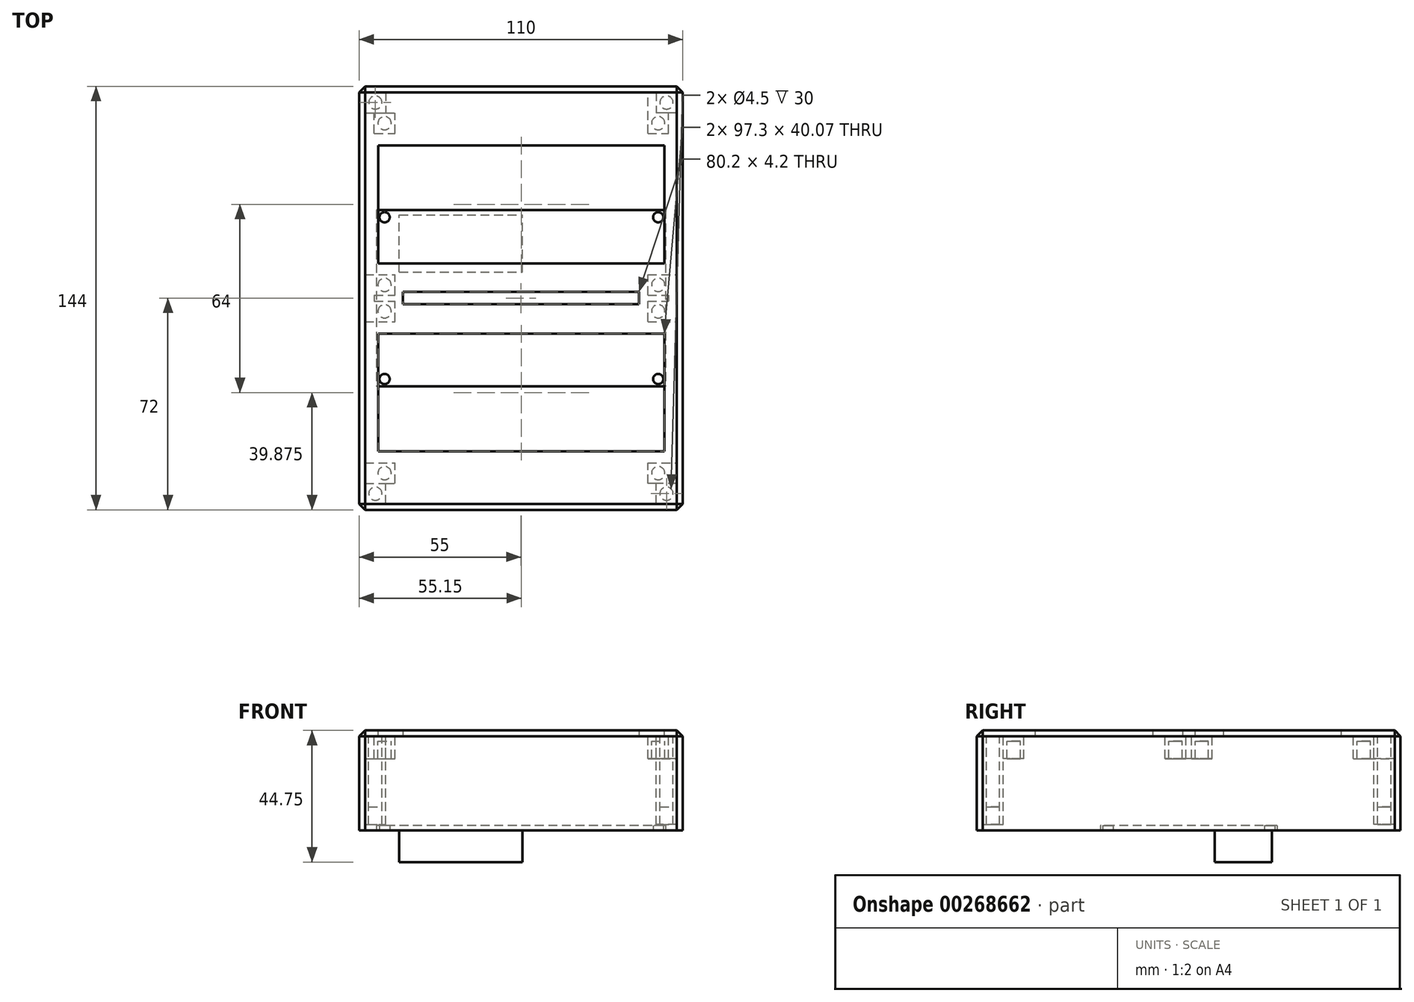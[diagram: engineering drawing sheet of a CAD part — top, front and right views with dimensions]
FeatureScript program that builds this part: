
annotation { "Feature Type Name" : "Feature", "Feature Type Description" : "" }
export const myFeature = defineFeature(function(context is Context, id is Id, definition is map)
    precondition{}
    {
        {
            var Q0;
            Q0=qCreatedBy(makeId("Top.planeOp"),FACE);
            var sketch = newSketch(context, id + "F0", { "sketchPlane" : qUnion([Q0])});
            skLineSegment(sketch, "E0.bottom", {"start": v(49.15, 30) * mm, "end": v(-49.15, 30) * mm});
            skLineSegment(sketch, "E0.top", {"start": v(49.15, -30) * mm, "end": v(-49.15, -30) * mm});
            skLineSegment(sketch, "E0.left", {"start": v(49.15, 30) * mm, "end": v(49.15, -30) * mm});
            skLineSegment(sketch, "E0.right", {"start": v(-49.15, 30) * mm, "end": v(-49.15, -30) * mm});
            skPoint(sketch, "E0.middle", {"position": v(0, 0) * mm});
            skCircle(sketch, "E1", {"center": v(46.65, 27.5) * mm, "radius": 1.75 * mm});
            skCircle(sketch, "E2.MirrorC", {"center": v(46.65, -27.5) * mm, "radius": 1.75 * mm});
            skCircle(sketch, "E3", {"center": v(-46.35, 27.5) * mm, "radius": 1.75 * mm});
            skCircle(sketch, "E4.MirrorC", {"center": v(-46.35, -27.5) * mm, "radius": 1.75 * mm});
            skSolve(sketch);
        }
        {
            var Q0;
            Q0=makeQuery(id+"F0.imprint","IMPRINT",FACE,{"disambiguationData":[TD([[makeQuery(id+"F0.imprint","IMPRINT",EDGE,{"derivedFrom":sQuery(id+"F0.wireOp",EDGE,"E0.bottom")}),1.0]])]});
            var Q1;
            Q1=makeQuery(id+"F0.imprint","IMPRINT",FACE,{"disambiguationData":[TD([[makeQuery(id+"F0.imprint","IMPRINT",EDGE,{"derivedFrom":sQuery(id+"F0.wireOp",EDGE,"rkxBa0un-ti2P-H2wi-MoX2-qtd8EblVNG1E.bottom")}),-1.0]])]});
            extrude(context, id + "F1", {"entities" : qUnion([Q0, Q1]), "depth" : 1.6 * mm});
        }
        {
            var Q0;
            Q0=makeQuery(id+"F1.opExtrude","CAP_FACE",FACE,{"disambiguationData":[OSD([sQuery(id+"F0.wireOp",EDGE,"E0.bottom"),sQuery(id+"F0.wireOp",EDGE,"E0.top"),sQuery(id+"F0.wireOp",EDGE,"E0.left"),sQuery(id+"F0.wireOp",EDGE,"E0.right"),sQuery(id+"F0.wireOp",EDGE,"E1"),sQuery(id+"F0.wireOp",EDGE,"E2.MirrorC"),sQuery(id+"F0.wireOp",EDGE,"E3"),sQuery(id+"F0.wireOp",EDGE,"E4.MirrorC")])],"isStart":false});
            var sketch = newSketch(context, id + "F2", { "sketchPlane" : qUnion([Q0])});
            skLineSegment(sketch, "E5.bottom", {"start": v(-48.4, 19.81) * mm, "end": v(48.7, 19.81) * mm});
            skLineSegment(sketch, "E5.top", {"start": v(-48.4, -20.06) * mm, "end": v(48.7, -20.06) * mm});
            skLineSegment(sketch, "E5.left", {"start": v(-48.4, 19.81) * mm, "end": v(-48.4, -20.06) * mm});
            skLineSegment(sketch, "E5.right", {"start": v(48.7, 19.81) * mm, "end": v(48.7, -20.06) * mm});
            skSolve(sketch);
        }
        {
            var Q0;
            Q0=makeQuery(id+"F2.imprint","IMPRINT",FACE,{"disambiguationData":[TD([[makeQuery(id+"F2.imprint","IMPRINT",EDGE,{"derivedFrom":sQuery(id+"F2.wireOp",EDGE,"E5.bottom")}),-1.0]])]});
            extrude(context, id + "F3", {"entities" : qUnion([Q0]), "depth" : 9.9 * mm});
        }
        {
            var Q0;
            Q0=makeQuery(id+"F0.imprint","IMPRINT",FACE,{"disambiguationData":[TD([[makeQuery(id+"F0.imprint","IMPRINT",EDGE,{"derivedFrom":sQuery(id+"F0.wireOp",EDGE,"E0.bottom")}),1.0]])]});
            var sketch = newSketch(context, id + "F4", { "sketchPlane" : qUnion([Q0])});
            skLineSegment(sketch, "E6.bottom", {"start": v(-41.35, 8.84) * mm, "end": v(0.58, 8.84) * mm});
            skLineSegment(sketch, "E6.top", {"start": v(-41.35, 28.34) * mm, "end": v(0.58, 28.34) * mm});
            skLineSegment(sketch, "E6.left", {"start": v(-41.35, 8.84) * mm, "end": v(-41.35, 28.34) * mm});
            skLineSegment(sketch, "E6.right", {"start": v(0.58, 8.84) * mm, "end": v(0.58, 28.34) * mm});
            skSolve(sketch);
        }
        {
            var Q0;
            Q0=makeQuery(id+"F4.imprint","IMPRINT",FACE,{"disambiguationData":[TD([[makeQuery(id+"F4.imprint","IMPRINT",EDGE,{"derivedFrom":sQuery(id+"F4.wireOp",EDGE,"E6.bottom")}),1.0]])]});
            extrude(context, id + "F5", {"entities" : qUnion([Q0]), "oppositeDirection" : true, "depth" : 10.75 * mm});
        }
        {
            var Q0;
            Q0=makeQuery(id+"F3.opExtrude","SWEPT_BODY",BODY,{"disambiguationData":[OSD([sQuery(id+"F2.wireOp",EDGE,"E5.bottom"),sQuery(id+"F2.wireOp",EDGE,"E5.top"),sQuery(id+"F2.wireOp",EDGE,"E5.left"),sQuery(id+"F2.wireOp",EDGE,"E5.right")])]});
            transform(context, id + "F6", {"entities" : qUnion([Q0]), "transformType" : TransformType.TRANSLATION_3D, "dx" : 0 * mm, "dy" : 0 * mm, "dz" : 0 * mm, "makeCopy" : true});
        }
        {
            var Q0;
            Q0=qCreatedBy(makeId("Top.planeOp"),FACE);
            var sketch = newSketch(context, id + "F7", { "sketchPlane" : qUnion([Q0])});
            skLineSegment(sketch, "E7.bottom", {"start": v(55, -72) * mm, "end": v(-55, -72) * mm});
            skLineSegment(sketch, "E7.top", {"start": v(55, 72) * mm, "end": v(-55, 72) * mm});
            skLineSegment(sketch, "E7.left", {"start": v(55, -72) * mm, "end": v(55, 72) * mm});
            skLineSegment(sketch, "E7.right", {"start": v(-55, -72) * mm, "end": v(-55, 72) * mm});
            skPoint(sketch, "E7.middle", {"position": v(0, 0) * mm});
            skSolve(sketch);
        }
        {
            var Q0;
            Q0 = qSketchRegion(id + "F7", true);
            extrude(context, id + "F8", {"entities" : qUnion([Q0]), "depth" : 34 * mm});
        }
        {
            var Q0;
            Q0=makeQuery(id+"F8.opExtrude","CAP_FACE",FACE,{"disambiguationData":[OSD([sQuery(id+"F7.wireOp",EDGE,"E7.bottom"),sQuery(id+"F7.wireOp",EDGE,"E7.top"),sQuery(id+"F7.wireOp",EDGE,"E7.left"),sQuery(id+"F7.wireOp",EDGE,"E7.right")])],"isStart":true});
            shell(context, id + "F9", {"entities" : qUnion([Q0]), "thickness" : 2 * mm});
        }
        {
            var Q0;
            Q0=makeQuery(id+"F8.opExtrude","CAP_FACE",FACE,{"disambiguationData":[OSD([sQuery(id+"F7.wireOp",EDGE,"E7.bottom"),sQuery(id+"F7.wireOp",EDGE,"E7.top"),sQuery(id+"F7.wireOp",EDGE,"E7.left"),sQuery(id+"F7.wireOp",EDGE,"E7.right")])],"isStart":false});
            var Q1;
            Q1=makeQuery(id+"F8.opExtrude","SWEPT_EDGE",EDGE,{"disambiguationData":[OSD([sQuery(id+"F7.wireOp",EDGE,"E7.bottom"),sQuery(id+"F7.wireOp",EDGE,"E7.left")])]});
            var Q2;
            Q2=makeQuery(id+"F8.opExtrude","SWEPT_EDGE",EDGE,{"disambiguationData":[OSD([sQuery(id+"F7.wireOp",EDGE,"E7.top"),sQuery(id+"F7.wireOp",EDGE,"E7.left")])]});
            var Q3;
            Q3=makeQuery(id+"F8.opExtrude","SWEPT_EDGE",EDGE,{"disambiguationData":[OSD([sQuery(id+"F7.wireOp",EDGE,"E7.top"),sQuery(id+"F7.wireOp",EDGE,"E7.right")])]});
            var Q4;
            Q4=makeQuery(id+"F8.opExtrude","SWEPT_EDGE",EDGE,{"disambiguationData":[OSD([sQuery(id+"F7.wireOp",EDGE,"E7.bottom"),sQuery(id+"F7.wireOp",EDGE,"E7.right")])]});
            chamfer(context, id + "F10", {"entities" : qUnion([Q0, Q1, Q2, Q3, Q4]), "width" : 2 * mm, "tangentPropagation" : true});
        }
        {
            var Q0;
            Q0=makeQuery(id+"F3.opExtrude","SWEPT_BODY",BODY,{"disambiguationData":[OSD([sQuery(id+"F2.wireOp",EDGE,"E5.bottom"),sQuery(id+"F2.wireOp",EDGE,"E5.top"),sQuery(id+"F2.wireOp",EDGE,"E5.left"),sQuery(id+"F2.wireOp",EDGE,"E5.right")])]});
            transform(context, id + "F11", {"entities" : qUnion([Q0]), "transformType" : TransformType.TRANSLATION_3D, "dx" : 0 * mm, "dy" : 32 * mm, "dz" : 22.4 * mm, "makeCopy" : false});
        }
        {
            var Q0;
            Q0=makeQuery(id+"F6.opPattern","COPY",BODY,{"derivedFrom":makeQuery(id+"F3.opExtrude","SWEPT_BODY",BODY,{"disambiguationData":[OSD([sQuery(id+"F2.wireOp",EDGE,"E5.bottom"),sQuery(id+"F2.wireOp",EDGE,"E5.top"),sQuery(id+"F2.wireOp",EDGE,"E5.left"),sQuery(id+"F2.wireOp",EDGE,"E5.right")])]}),"instanceName":"1"});
            transform(context, id + "F12", {"entities" : qUnion([Q0]), "transformType" : TransformType.TRANSLATION_3D, "dx" : 0 * mm, "dy" : -32 * mm, "dz" : 22.4 * mm, "makeCopy" : false});
        }
        {
            var Q0;
            Q0=makeQuery(id+"F8.opExtrude","CAP_FACE",FACE,{"disambiguationData":[OSD([sQuery(id+"F7.wireOp",EDGE,"E7.bottom"),sQuery(id+"F7.wireOp",EDGE,"E7.top"),sQuery(id+"F7.wireOp",EDGE,"E7.left"),sQuery(id+"F7.wireOp",EDGE,"E7.right")])],"isStart":false});
            cPlane(context, id + "F13", {"entities" : qUnion([Q0]), "cplaneType" : CPlaneType.OFFSET, "offset" : 0 * mm, "width" : 150 * mm, "height" : 150 * mm});
        }
        {
            var Q0;
            Q0=qCreatedBy(id+"F13.planeOp",FACE);
            var sketch = newSketch(context, id + "F14", { "sketchPlane" : qUnion([Q0])});
            skLineSegment(sketch, "E8.0.0", {"start": v(-48.4, 51.81) * mm, "end": v(-48.4, 11.94) * mm});
            skLineSegment(sketch, "E8.0.1", {"start": v(-48.4, 11.94) * mm, "end": v(48.7, 11.94) * mm});
            skLineSegment(sketch, "E8.0.2", {"start": v(48.7, 11.94) * mm, "end": v(48.7, 51.81) * mm});
            skLineSegment(sketch, "E8.0.3", {"start": v(48.7, 51.81) * mm, "end": v(-48.4, 51.81) * mm});
            skLineSegment(sketch, "E9.0.0", {"start": v(-48.4, -12.19) * mm, "end": v(-48.4, -52.06) * mm});
            skLineSegment(sketch, "E9.0.1", {"start": v(-48.4, -52.06) * mm, "end": v(48.7, -52.06) * mm});
            skLineSegment(sketch, "E9.0.2", {"start": v(48.7, -52.06) * mm, "end": v(48.7, -12.19) * mm});
            skLineSegment(sketch, "E9.0.3", {"start": v(48.7, -12.19) * mm, "end": v(-48.4, -12.19) * mm});
            skCircle(sketch, "E10.0", {"center": v(-46.35, -4.5) * mm, "radius": 1.75 * mm});
            skCircle(sketch, "E11.0", {"center": v(-46.35, 4.5) * mm, "radius": 1.75 * mm});
            skCircle(sketch, "E12.0", {"center": v(46.65, 4.5) * mm, "radius": 1.75 * mm});
            skCircle(sketch, "E13.0", {"center": v(46.65, -4.5) * mm, "radius": 1.75 * mm});
            skCircle(sketch, "E14.0", {"center": v(46.65, -59.5) * mm, "radius": 1.75 * mm});
            skCircle(sketch, "E15.0", {"center": v(-46.35, -59.5) * mm, "radius": 1.75 * mm});
            skCircle(sketch, "E16.0", {"center": v(-46.35, 59.5) * mm, "radius": 1.75 * mm});
            skCircle(sketch, "E17.0", {"center": v(46.65, 59.5) * mm, "radius": 1.75 * mm});
            skLineSegment(sketch, "E18.MirrorCS", {"start": v(48.7, 91.68) * mm, "end": v(48.7, 51.81) * mm});
            skLineSegment(sketch, "E19.0", {"start": v(48.8, 51.91) * mm, "end": v(-48.5, 51.91) * mm});
            skLineSegment(sketch, "E19.1", {"start": v(48.8, 11.84) * mm, "end": v(48.8, 51.91) * mm});
            skLineSegment(sketch, "E19.2", {"start": v(-48.5, 11.84) * mm, "end": v(48.8, 11.84) * mm});
            skLineSegment(sketch, "E19.3", {"start": v(-48.5, 51.91) * mm, "end": v(-48.5, 11.84) * mm});
            skLineSegment(sketch, "E20.0", {"start": v(48.8, -12.09) * mm, "end": v(-48.5, -12.09) * mm});
            skLineSegment(sketch, "E20.1", {"start": v(48.8, -52.16) * mm, "end": v(48.8, -12.09) * mm});
            skLineSegment(sketch, "E20.2", {"start": v(-48.5, -52.16) * mm, "end": v(48.8, -52.16) * mm});
            skLineSegment(sketch, "E20.3", {"start": v(-48.5, -12.09) * mm, "end": v(-48.5, -52.16) * mm});
            skSolve(sketch);
        }
        {
            var Q0;
            Q0=makeQuery(id+"F14.imprint","IMPRINT",FACE,{"disambiguationData":[TD([[makeQuery(id+"F14.imprint","IMPRINT",EDGE,{"derivedFrom":sQuery(id+"F14.wireOp",EDGE,"E8.0.0")}),-1.0]])]});
            var Q1;
            Q1=makeQuery(id+"F14.imprint","IMPRINT",FACE,{"disambiguationData":[TD([[makeQuery(id+"F14.imprint","IMPRINT",EDGE,{"derivedFrom":sQuery(id+"F14.wireOp",EDGE,"E8.0.0")}),1.0]])]});
            var Q2;
            Q2=makeQuery(id+"F14.imprint","IMPRINT",FACE,{"disambiguationData":[TD([[makeQuery(id+"F14.imprint","IMPRINT",EDGE,{"derivedFrom":sQuery(id+"F14.wireOp",EDGE,"E9.0.0")}),-1.0]])]});
            var Q3;
            Q3=makeQuery(id+"F14.imprint","IMPRINT",FACE,{"disambiguationData":[TD([[makeQuery(id+"F14.imprint","IMPRINT",EDGE,{"derivedFrom":sQuery(id+"F14.wireOp",EDGE,"E9.0.0")}),1.0]])]});
            var Q4;
            Q4=sQuery(id+"F14.wireOp",EDGE,"E19.3");
            var Q5;
            Q5=sQuery(id+"F14.wireOp",EDGE,"E19.2");
            var Q6;
            Q6=sQuery(id+"F14.wireOp",EDGE,"E19.1");
            var Q7;
            Q7=sQuery(id+"F14.wireOp",EDGE,"E19.0");
            extrude(context, id + "F15", {"entities" : qUnion([Q0, Q1, Q2, Q3]), "operationType" : NewBodyOperationType.REMOVE, "surfaceEntities" : qUnion([Q4, Q5, Q6, Q7]), "oppositeDirection" : true, "depth" : 25 * mm});
        }
        {
            var Q0;
            Q0=makeQuery(id+"F9.opShell","OFFSET_FACE",FACE,{"disambiguationData":[OSD([sQuery(id+"F7.wireOp",EDGE,"E7.bottom"),sQuery(id+"F7.wireOp",EDGE,"E7.top"),sQuery(id+"F7.wireOp",EDGE,"E7.left"),sQuery(id+"F7.wireOp",EDGE,"E7.right")])]});
            cPlane(context, id + "F16", {"entities" : qUnion([Q0]), "cplaneType" : CPlaneType.OFFSET, "offset" : 0 * mm, "width" : 150 * mm, "height" : 150 * mm});
        }
        {
            var Q0;
            Q0=qCreatedBy(id+"F16.planeOp",FACE);
            var sketch = newSketch(context, id + "F17", { "sketchPlane" : qUnion([Q0])});
            skLineSegment(sketch, "E21.bottom", {"start": v(-53, 70) * mm, "end": v(-46, 70) * mm});
            skLineSegment(sketch, "E21.top", {"start": v(-53, 63) * mm, "end": v(-46, 63) * mm});
            skLineSegment(sketch, "E21.left", {"start": v(-53, 70) * mm, "end": v(-53, 63) * mm});
            skLineSegment(sketch, "E21.right", {"start": v(-46, 70) * mm, "end": v(-46, 63) * mm});
            skLineSegment(sketch, "E22.MirrorCS", {"start": v(46, 70) * mm, "end": v(46, 63) * mm});
            skLineSegment(sketch, "E23.MirrorCS", {"start": v(53, 70) * mm, "end": v(46, 70) * mm});
            skLineSegment(sketch, "E24.MirrorCS", {"start": v(53, 70) * mm, "end": v(53, 63) * mm});
            skLineSegment(sketch, "E25.MirrorCS", {"start": v(53, 63) * mm, "end": v(46, 63) * mm});
            skLineSegment(sketch, "E26.MirrorCS", {"start": v(-53, -63) * mm, "end": v(-46, -63) * mm});
            skLineSegment(sketch, "E27.MirrorCS", {"start": v(-53, -70) * mm, "end": v(-53, -63) * mm});
            skLineSegment(sketch, "E28.MirrorCS", {"start": v(-53, -70) * mm, "end": v(-46, -70) * mm});
            skLineSegment(sketch, "E29.MirrorCS", {"start": v(-46, -70) * mm, "end": v(-46, -63) * mm});
            skLineSegment(sketch, "E30.MirrorCS", {"start": v(46, -70) * mm, "end": v(46, -63) * mm});
            skLineSegment(sketch, "E31.MirrorCS", {"start": v(53, -70) * mm, "end": v(46, -70) * mm});
            skLineSegment(sketch, "E32.MirrorCS", {"start": v(53, -70) * mm, "end": v(53, -63) * mm});
            skLineSegment(sketch, "E33.MirrorCS", {"start": v(53, -63) * mm, "end": v(46, -63) * mm});
            skCircle(sketch, "E34", {"center": v(49.5, -66.5) * mm, "radius": 2.25 * mm});
            skCircle(sketch, "E35.MirrorC", {"center": v(-49.5, -66.5) * mm, "radius": 2.25 * mm});
            skCircle(sketch, "E36.MirrorC", {"center": v(49.5, 66.5) * mm, "radius": 2.25 * mm});
            skCircle(sketch, "E37.MirrorC", {"center": v(-49.5, 66.5) * mm, "radius": 2.25 * mm});
            skLineSegment(sketch, "E38.bottom", {"start": v(43.15, -56) * mm, "end": v(50.15, -56) * mm});
            skLineSegment(sketch, "E38.top", {"start": v(43.15, -63) * mm, "end": v(50.15, -63) * mm});
            skLineSegment(sketch, "E38.left", {"start": v(43.15, -56) * mm, "end": v(43.15, -63) * mm});
            skLineSegment(sketch, "E38.right", {"start": v(50.15, -56) * mm, "end": v(50.15, -63) * mm});
            skPoint(sketch, "E38.middle", {"position": v(46.65, -59.5) * mm});
            skLineSegment(sketch, "E39.bottom", {"start": v(-49.85, -56) * mm, "end": v(-42.85, -56) * mm});
            skLineSegment(sketch, "E39.top", {"start": v(-49.85, -63) * mm, "end": v(-42.85, -63) * mm});
            skLineSegment(sketch, "E39.left", {"start": v(-49.85, -56) * mm, "end": v(-49.85, -63) * mm});
            skLineSegment(sketch, "E39.right", {"start": v(-42.85, -56) * mm, "end": v(-42.85, -63) * mm});
            skPoint(sketch, "E39.middle", {"position": v(-46.35, -59.5) * mm});
            skLineSegment(sketch, "E40.bottom", {"start": v(-49.85, -1) * mm, "end": v(-42.85, -1) * mm});
            skLineSegment(sketch, "E40.top", {"start": v(-49.85, -8) * mm, "end": v(-42.85, -8) * mm});
            skLineSegment(sketch, "E40.left", {"start": v(-49.85, -1) * mm, "end": v(-49.85, -8) * mm});
            skLineSegment(sketch, "E40.right", {"start": v(-42.85, -1) * mm, "end": v(-42.85, -8) * mm});
            skPoint(sketch, "E40.middle", {"position": v(-46.35, -4.5) * mm});
            skLineSegment(sketch, "E41.bottom", {"start": v(-49.85, 8) * mm, "end": v(-42.85, 8) * mm});
            skLineSegment(sketch, "E41.top", {"start": v(-49.85, 1) * mm, "end": v(-42.85, 1) * mm});
            skLineSegment(sketch, "E41.left", {"start": v(-49.85, 8) * mm, "end": v(-49.85, 1) * mm});
            skLineSegment(sketch, "E41.right", {"start": v(-42.85, 8) * mm, "end": v(-42.85, 1) * mm});
            skPoint(sketch, "E41.middle", {"position": v(-46.35, 4.5) * mm});
            skLineSegment(sketch, "E42.bottom", {"start": v(43.15, -1) * mm, "end": v(50.15, -1) * mm});
            skLineSegment(sketch, "E42.top", {"start": v(43.15, -8) * mm, "end": v(50.15, -8) * mm});
            skLineSegment(sketch, "E42.left", {"start": v(43.15, -1) * mm, "end": v(43.15, -8) * mm});
            skLineSegment(sketch, "E42.right", {"start": v(50.15, -1) * mm, "end": v(50.15, -8) * mm});
            skPoint(sketch, "E42.middle", {"position": v(46.65, -4.5) * mm});
            skLineSegment(sketch, "E43.bottom", {"start": v(43.15, 8) * mm, "end": v(50.15, 8) * mm});
            skLineSegment(sketch, "E43.top", {"start": v(43.15, 1) * mm, "end": v(50.15, 1) * mm});
            skLineSegment(sketch, "E43.left", {"start": v(43.15, 8) * mm, "end": v(43.15, 1) * mm});
            skLineSegment(sketch, "E43.right", {"start": v(50.15, 8) * mm, "end": v(50.15, 1) * mm});
            skPoint(sketch, "E43.middle", {"position": v(46.65, 4.5) * mm});
            skLineSegment(sketch, "E44.bottom", {"start": v(-49.85, 63) * mm, "end": v(-42.85, 63) * mm});
            skLineSegment(sketch, "E44.top", {"start": v(-49.85, 56) * mm, "end": v(-42.85, 56) * mm});
            skLineSegment(sketch, "E44.left", {"start": v(-49.85, 63) * mm, "end": v(-49.85, 56) * mm});
            skLineSegment(sketch, "E44.right", {"start": v(-42.85, 63) * mm, "end": v(-42.85, 56) * mm});
            skPoint(sketch, "E44.middle", {"position": v(-46.35, 59.5) * mm});
            skLineSegment(sketch, "E45.bottom", {"start": v(43.15, 63) * mm, "end": v(50.15, 63) * mm});
            skLineSegment(sketch, "E45.top", {"start": v(43.15, 56) * mm, "end": v(50.15, 56) * mm});
            skLineSegment(sketch, "E45.left", {"start": v(43.15, 63) * mm, "end": v(43.15, 56) * mm});
            skLineSegment(sketch, "E45.right", {"start": v(50.15, 63) * mm, "end": v(50.15, 56) * mm});
            skPoint(sketch, "E45.middle", {"position": v(46.65, 59.5) * mm});
            skCircle(sketch, "E46", {"center": v(46.65, -59.5) * mm, "radius": 2.25 * mm});
            skCircle(sketch, "E47", {"center": v(-46.35, -59.5) * mm, "radius": 2.25 * mm});
            skCircle(sketch, "E48", {"center": v(-46.35, -4.5) * mm, "radius": 2.25 * mm});
            skCircle(sketch, "E49", {"center": v(-46.35, 4.5) * mm, "radius": 2.25 * mm});
            skCircle(sketch, "E50", {"center": v(46.65, 4.5) * mm, "radius": 2.25 * mm});
            skCircle(sketch, "E51", {"center": v(46.65, -4.5) * mm, "radius": 2.25 * mm});
            skCircle(sketch, "E52", {"center": v(46.65, 59.5) * mm, "radius": 2.25 * mm});
            skCircle(sketch, "E53", {"center": v(-46.35, 59.5) * mm, "radius": 2.25 * mm});
            skLineSegment(sketch, "E54.bottom", {"start": v(46, -70) * mm, "end": v(43.15, -70) * mm});
            skLineSegment(sketch, "E54.top", {"start": v(46, -63) * mm, "end": v(43.15, -63) * mm});
            skLineSegment(sketch, "E54.right", {"start": v(43.15, -70) * mm, "end": v(43.15, -63) * mm});
            skLineSegment(sketch, "E55.bottom", {"start": v(53, -63) * mm, "end": v(50.15, -63) * mm});
            skLineSegment(sketch, "E55.top", {"start": v(53, -56) * mm, "end": v(50.15, -56) * mm});
            skLineSegment(sketch, "E55.left", {"start": v(53, -63) * mm, "end": v(53, -56) * mm});
            skLineSegment(sketch, "E55.right", {"start": v(50.15, -63) * mm, "end": v(50.15, -56) * mm});
            skLineSegment(sketch, "E56.bottom", {"start": v(-42.85, -63) * mm, "end": v(-46, -63) * mm});
            skLineSegment(sketch, "E56.top", {"start": v(-42.85, -70) * mm, "end": v(-46, -70) * mm});
            skLineSegment(sketch, "E56.left", {"start": v(-42.85, -63) * mm, "end": v(-42.85, -70) * mm});
            skLineSegment(sketch, "E56.right", {"start": v(-46, -63) * mm, "end": v(-46, -70) * mm});
            skLineSegment(sketch, "E57.bottom", {"start": v(-53, -63) * mm, "end": v(-49.85, -63) * mm});
            skLineSegment(sketch, "E57.top", {"start": v(-53, -56) * mm, "end": v(-49.85, -56) * mm});
            skLineSegment(sketch, "E57.left", {"start": v(-53, -63) * mm, "end": v(-53, -56) * mm});
            skLineSegment(sketch, "E57.right", {"start": v(-49.85, -63) * mm, "end": v(-49.85, -56) * mm});
            skLineSegment(sketch, "E58.bottom", {"start": v(-49.85, -8) * mm, "end": v(-53, -8) * mm});
            skLineSegment(sketch, "E58.top", {"start": v(-49.85, 8) * mm, "end": v(-53, 8) * mm});
            skLineSegment(sketch, "E58.left", {"start": v(-49.85, -8) * mm, "end": v(-49.85, 8) * mm});
            skLineSegment(sketch, "E58.right", {"start": v(-53, -8) * mm, "end": v(-53, 8) * mm});
            skLineSegment(sketch, "E59.bottom", {"start": v(-42.85, -1) * mm, "end": v(-49.85, -1) * mm});
            skLineSegment(sketch, "E59.top", {"start": v(-42.85, 1) * mm, "end": v(-49.85, 1) * mm});
            skLineSegment(sketch, "E59.left", {"start": v(-42.85, -1) * mm, "end": v(-42.85, 1) * mm});
            skLineSegment(sketch, "E59.right", {"start": v(-49.85, -1) * mm, "end": v(-49.85, 1) * mm});
            skLineSegment(sketch, "E60.bottom", {"start": v(50.15, -8) * mm, "end": v(53, -8) * mm});
            skLineSegment(sketch, "E60.top", {"start": v(50.15, 8) * mm, "end": v(53, 8) * mm});
            skLineSegment(sketch, "E60.left", {"start": v(50.15, -8) * mm, "end": v(50.15, 8) * mm});
            skLineSegment(sketch, "E60.right", {"start": v(53, -8) * mm, "end": v(53, 8) * mm});
            skLineSegment(sketch, "E61.bottom", {"start": v(50.15, -1) * mm, "end": v(43.15, -1) * mm});
            skLineSegment(sketch, "E61.top", {"start": v(50.15, 1) * mm, "end": v(43.15, 1) * mm});
            skLineSegment(sketch, "E61.left", {"start": v(50.15, -1) * mm, "end": v(50.15, 1) * mm});
            skLineSegment(sketch, "E61.right", {"start": v(43.15, -1) * mm, "end": v(43.15, 1) * mm});
            skLineSegment(sketch, "E62.bottom", {"start": v(43.15, 63) * mm, "end": v(46, 63) * mm});
            skLineSegment(sketch, "E62.top", {"start": v(43.15, 70) * mm, "end": v(46, 70) * mm});
            skLineSegment(sketch, "E62.left", {"start": v(43.15, 63) * mm, "end": v(43.15, 70) * mm});
            skLineSegment(sketch, "E62.right", {"start": v(46, 63) * mm, "end": v(46, 70) * mm});
            skLineSegment(sketch, "E63.bottom", {"start": v(50.15, 56) * mm, "end": v(53, 56) * mm});
            skLineSegment(sketch, "E63.top", {"start": v(50.15, 63) * mm, "end": v(53, 63) * mm});
            skLineSegment(sketch, "E63.left", {"start": v(50.15, 56) * mm, "end": v(50.15, 63) * mm});
            skLineSegment(sketch, "E63.right", {"start": v(53, 56) * mm, "end": v(53, 63) * mm});
            skLineSegment(sketch, "E64.bottom", {"start": v(-49.85, 56) * mm, "end": v(-53, 56) * mm});
            skLineSegment(sketch, "E64.top", {"start": v(-49.85, 63) * mm, "end": v(-53, 63) * mm});
            skLineSegment(sketch, "E64.left", {"start": v(-49.85, 56) * mm, "end": v(-49.85, 63) * mm});
            skLineSegment(sketch, "E64.right", {"start": v(-53, 56) * mm, "end": v(-53, 63) * mm});
            skLineSegment(sketch, "E65.bottom", {"start": v(-42.85, 63) * mm, "end": v(-46, 63) * mm});
            skLineSegment(sketch, "E65.top", {"start": v(-42.85, 70) * mm, "end": v(-46, 70) * mm});
            skLineSegment(sketch, "E65.left", {"start": v(-42.85, 63) * mm, "end": v(-42.85, 70) * mm});
            skLineSegment(sketch, "E65.right", {"start": v(-46, 63) * mm, "end": v(-46, 70) * mm});
            skLineSegment(sketch, "E66.bottom", {"start": v(-40.1, -2.1) * mm, "end": v(40.1, -2.1) * mm});
            skLineSegment(sketch, "E66.top", {"start": v(-40.1, 2.1) * mm, "end": v(40.1, 2.1) * mm});
            skLineSegment(sketch, "E66.left", {"start": v(-40.1, -2.1) * mm, "end": v(-40.1, 2.1) * mm});
            skLineSegment(sketch, "E66.right", {"start": v(40.1, -2.1) * mm, "end": v(40.1, 2.1) * mm});
            skPoint(sketch, "E66.middle", {"position": v(0, 0) * mm});
            skSolve(sketch);
        }
        {
            var Q0;
            Q0=makeQuery(id+"F17.imprint","IMPRINT",FACE,{"disambiguationData":[TD([[makeQuery(id+"F17.imprint","IMPRINT",EDGE,{"derivedFrom":sQuery(id+"F17.wireOp",EDGE,"E21.bottom")}),-1.0]])]});
            var Q1;
            Q1=makeQuery(id+"F17.imprint","IMPRINT",FACE,{"disambiguationData":[TD([[makeQuery(id+"F17.imprint","IMPRINT",EDGE,{"derivedFrom":sQuery(id+"F17.wireOp",EDGE,"E22.MirrorCS")}),1.0]])]});
            var Q2;
            Q2=makeQuery(id+"F17.imprint","IMPRINT",FACE,{"disambiguationData":[TD([[makeQuery(id+"F17.imprint","IMPRINT",EDGE,{"derivedFrom":sQuery(id+"F17.wireOp",EDGE,"E26.MirrorCS")}),-1.0]])]});
            var Q3;
            Q3=makeQuery(id+"F17.imprint","IMPRINT",FACE,{"disambiguationData":[TD([[makeQuery(id+"F17.imprint","IMPRINT",EDGE,{"derivedFrom":sQuery(id+"F17.wireOp",EDGE,"E30.MirrorCS")}),-1.0]])]});
            var Q4;
            Q4=makeQuery(id+"F17.imprint","IMPRINT",FACE,{"disambiguationData":[TD([[makeQuery(id+"F17.imprint","IMPRINT",EDGE,{"derivedFrom":sQuery(id+"F17.wireOp",EDGE,"E31.MirrorCS")}),-1.0]])]});
            var Q5;
            Q5=makeQuery(id+"F17.imprint","IMPRINT",FACE,{"disambiguationData":[TD([[makeQuery(id+"F17.imprint","IMPRINT",EDGE,{"derivedFrom":sQuery(id+"F17.wireOp",EDGE,"E27.MirrorCS")}),-1.0]])]});
            var Q6;
            Q6=makeQuery(id+"F17.imprint","IMPRINT",FACE,{"disambiguationData":[TD([[makeQuery(id+"F17.imprint","IMPRINT",EDGE,{"derivedFrom":sQuery(id+"F17.wireOp",EDGE,"E23.MirrorCS")}),1.0]])]});
            extrude(context, id + "F18", {"entities" : qUnion([Q0, Q1, Q2, Q3, Q4, Q5, Q6]), "operationType" : NewBodyOperationType.ADD, "depth" : 30 * mm});
        }
        {
            var Q0;
            Q0=makeQuery(id+"F17.imprint","IMPRINT",FACE,{"disambiguationData":[TD([[makeQuery(id+"F17.imprint","IMPRINT",EDGE,{"derivedFrom":sQuery(id+"F17.wireOp",EDGE,"E35.MirrorC")}),-1.0]])]});
            var Q1;
            Q1=makeQuery(id+"F17.imprint","IMPRINT",FACE,{"disambiguationData":[TD([[makeQuery(id+"F17.imprint","IMPRINT",EDGE,{"derivedFrom":sQuery(id+"F17.wireOp",EDGE,"E34")}),1.0]])]});
            var Q2;
            Q2=makeQuery(id+"F17.imprint","IMPRINT",FACE,{"disambiguationData":[TD([[makeQuery(id+"F17.imprint","IMPRINT",EDGE,{"derivedFrom":sQuery(id+"F17.wireOp",EDGE,"E36.MirrorC")}),-1.0]])]});
            var Q3;
            Q3=makeQuery(id+"F17.imprint","IMPRINT",FACE,{"disambiguationData":[TD([[makeQuery(id+"F17.imprint","IMPRINT",EDGE,{"derivedFrom":sQuery(id+"F17.wireOp",EDGE,"E37.MirrorC")}),1.0]])]});
            var Q4;
            Q4=sQuery(id+"F17.wireOp",EDGE,"E35.MirrorC");
            extrude(context, id + "F19", {"entities" : qUnion([Q0, Q1, Q2, Q3]), "operationType" : NewBodyOperationType.ADD, "surfaceEntities" : qUnion([Q4]), "depth" : 24 * mm});
        }
        {
            var Q0;
            Q0=makeQuery(id+"F17.imprint","IMPRINT",FACE,{"disambiguationData":[TD([[makeQuery(id+"F17.imprint","IMPRINT",EDGE,{"derivedFrom":sQuery(id+"F17.wireOp",EDGE,"E44.bottom")}),-1.0]])]});
            var Q1;
            Q1=makeQuery(id+"F17.imprint","IMPRINT",FACE,{"disambiguationData":[TD([[makeQuery(id+"F17.imprint","IMPRINT",EDGE,{"derivedFrom":sQuery(id+"F17.wireOp",EDGE,"E41.bottom")}),-1.0]])]});
            var Q2;
            Q2=makeQuery(id+"F17.imprint","IMPRINT",FACE,{"disambiguationData":[TD([[makeQuery(id+"F17.imprint","IMPRINT",EDGE,{"derivedFrom":sQuery(id+"F17.wireOp",EDGE,"E40.bottom")}),-1.0]])]});
            var Q3;
            Q3=makeQuery(id+"F17.imprint","IMPRINT",FACE,{"disambiguationData":[TD([[makeQuery(id+"F17.imprint","IMPRINT",EDGE,{"derivedFrom":sQuery(id+"F17.wireOp",EDGE,"E45.bottom")}),-1.0]])]});
            var Q4;
            Q4=makeQuery(id+"F17.imprint","IMPRINT",FACE,{"disambiguationData":[TD([[makeQuery(id+"F17.imprint","IMPRINT",EDGE,{"derivedFrom":sQuery(id+"F17.wireOp",EDGE,"E43.bottom")}),-1.0]])]});
            var Q5;
            Q5=makeQuery(id+"F17.imprint","IMPRINT",FACE,{"disambiguationData":[TD([[makeQuery(id+"F17.imprint","IMPRINT",EDGE,{"derivedFrom":sQuery(id+"F17.wireOp",EDGE,"E42.bottom")}),-1.0]])]});
            var Q6;
            Q6=makeQuery(id+"F17.imprint","IMPRINT",FACE,{"disambiguationData":[TD([[makeQuery(id+"F17.imprint","IMPRINT",EDGE,{"derivedFrom":sQuery(id+"F17.wireOp",EDGE,"E38.bottom")}),-1.0]])]});
            var Q7;
            Q7=makeQuery(id+"F17.imprint","IMPRINT",FACE,{"disambiguationData":[TD([[makeQuery(id+"F17.imprint","IMPRINT",EDGE,{"derivedFrom":sQuery(id+"F17.wireOp",EDGE,"E39.bottom")}),-1.0]])]});
            var Q8;
            Q8=makeQuery(id+"F17.imprint","IMPRINT",FACE,{"disambiguationData":[TD([[makeQuery(id+"F17.imprint","IMPRINT",EDGE,{"derivedFrom":sQuery(id+"F17.wireOp",EDGE,"E54.bottom")}),-1.0]])]});
            var Q9;
            Q9=makeQuery(id+"F17.imprint","IMPRINT",FACE,{"disambiguationData":[TD([[makeQuery(id+"F17.imprint","IMPRINT",EDGE,{"derivedFrom":sQuery(id+"F17.wireOp",EDGE,"E55.bottom")}),-1.0]])]});
            var Q10;
            Q10=makeQuery(id+"F17.imprint","IMPRINT",FACE,{"disambiguationData":[TD([[makeQuery(id+"F17.imprint","IMPRINT",EDGE,{"derivedFrom":sQuery(id+"F17.wireOp",EDGE,"E57.bottom")}),1.0]])]});
            var Q11;
            Q11=makeQuery(id+"F17.imprint","IMPRINT",FACE,{"disambiguationData":[TD([[makeQuery(id+"F17.imprint","IMPRINT",EDGE,{"derivedFrom":sQuery(id+"F17.wireOp",EDGE,"E56.bottom")}),1.0]])]});
            var Q12;
            {var subQ1=sQuery(id+"F17.wireOp",EDGE,"E40.top");Q12=makeQuery(id+"F17.imprint","IMPRINT",FACE,{"disambiguationData":[TD([[makeQuery(id+"F17.imprint","IMPRINT",EDGE,{"derivedFrom":subQ1}),1.0]])]});}
            var Q13;
            {var subQ3=sQuery(id+"F17.wireOp",EDGE,"E58.bottom");Q13=makeQuery(id+"F17.imprint","IMPRINT",FACE,{"disambiguationData":[TD([[makeQuery(id+"F17.imprint","IMPRINT",EDGE,{"derivedFrom":subQ3}),-1.0]])]});}
            var Q14;
            Q14=makeQuery(id+"F17.imprint","IMPRINT",FACE,{"disambiguationData":[TD([[makeQuery(id+"F17.imprint","IMPRINT",EDGE,{"derivedFrom":sQuery(id+"F17.wireOp",EDGE,"E59.bottom")}),-1.0]])]});
            var Q15;
            {var subQ1=sQuery(id+"F17.wireOp",EDGE,"E42.top");Q15=makeQuery(id+"F17.imprint","IMPRINT",FACE,{"disambiguationData":[TD([[makeQuery(id+"F17.imprint","IMPRINT",EDGE,{"derivedFrom":subQ1}),1.0]])]});}
            var Q16;
            Q16=makeQuery(id+"F17.imprint","IMPRINT",FACE,{"disambiguationData":[TD([[makeQuery(id+"F17.imprint","IMPRINT",EDGE,{"derivedFrom":sQuery(id+"F17.wireOp",EDGE,"E61.bottom")}),-1.0]])]});
            var Q17;
            {var subQ3=sQuery(id+"F17.wireOp",EDGE,"E60.bottom");Q17=makeQuery(id+"F17.imprint","IMPRINT",FACE,{"disambiguationData":[TD([[makeQuery(id+"F17.imprint","IMPRINT",EDGE,{"derivedFrom":subQ3}),1.0]])]});}
            var Q18;
            Q18=makeQuery(id+"F17.imprint","IMPRINT",FACE,{"disambiguationData":[TD([[makeQuery(id+"F17.imprint","IMPRINT",EDGE,{"derivedFrom":sQuery(id+"F17.wireOp",EDGE,"E62.bottom")}),1.0]])]});
            var Q19;
            Q19=makeQuery(id+"F17.imprint","IMPRINT",FACE,{"disambiguationData":[TD([[makeQuery(id+"F17.imprint","IMPRINT",EDGE,{"derivedFrom":sQuery(id+"F17.wireOp",EDGE,"E63.bottom")}),1.0]])]});
            var Q20;
            Q20=makeQuery(id+"F17.imprint","IMPRINT",FACE,{"disambiguationData":[TD([[makeQuery(id+"F17.imprint","IMPRINT",EDGE,{"derivedFrom":sQuery(id+"F17.wireOp",EDGE,"E64.bottom")}),-1.0]])]});
            var Q21;
            Q21=makeQuery(id+"F17.imprint","IMPRINT",FACE,{"disambiguationData":[TD([[makeQuery(id+"F17.imprint","IMPRINT",EDGE,{"derivedFrom":sQuery(id+"F17.wireOp",EDGE,"E65.bottom")}),-1.0]])]});
            extrude(context, id + "F20", {"entities" : qUnion([Q0, Q1, Q2, Q3, Q4, Q5, Q6, Q7, Q8, Q9, Q10, Q11, Q12, Q13, Q14, Q15, Q16, Q17, Q18, Q19, Q20, Q21]), "operationType" : NewBodyOperationType.ADD, "depth" : 7.6 * mm});
        }
        {
            var Q0;
            Q0=makeQuery(id+"F17.imprint","IMPRINT",FACE,{"disambiguationData":[TD([[makeQuery(id+"F17.imprint","IMPRINT",EDGE,{"derivedFrom":sQuery(id+"F17.wireOp",EDGE,"E53")}),1.0]])]});
            var Q1;
            Q1=makeQuery(id+"F17.imprint","IMPRINT",FACE,{"disambiguationData":[TD([[makeQuery(id+"F17.imprint","IMPRINT",EDGE,{"derivedFrom":sQuery(id+"F17.wireOp",EDGE,"E52")}),1.0]])]});
            var Q2;
            Q2=makeQuery(id+"F17.imprint","IMPRINT",FACE,{"disambiguationData":[TD([[makeQuery(id+"F17.imprint","IMPRINT",EDGE,{"derivedFrom":sQuery(id+"F17.wireOp",EDGE,"E50")}),1.0]])]});
            var Q3;
            Q3=makeQuery(id+"F17.imprint","IMPRINT",FACE,{"disambiguationData":[TD([[makeQuery(id+"F17.imprint","IMPRINT",EDGE,{"derivedFrom":sQuery(id+"F17.wireOp",EDGE,"E51")}),1.0]])]});
            var Q4;
            Q4=makeQuery(id+"F17.imprint","IMPRINT",FACE,{"disambiguationData":[TD([[makeQuery(id+"F17.imprint","IMPRINT",EDGE,{"derivedFrom":sQuery(id+"F17.wireOp",EDGE,"E48")}),1.0]])]});
            var Q5;
            Q5=makeQuery(id+"F17.imprint","IMPRINT",FACE,{"disambiguationData":[TD([[makeQuery(id+"F17.imprint","IMPRINT",EDGE,{"derivedFrom":sQuery(id+"F17.wireOp",EDGE,"E49")}),1.0]])]});
            var Q6;
            Q6=makeQuery(id+"F17.imprint","IMPRINT",FACE,{"disambiguationData":[TD([[makeQuery(id+"F17.imprint","IMPRINT",EDGE,{"derivedFrom":sQuery(id+"F17.wireOp",EDGE,"E46")}),1.0]])]});
            var Q7;
            Q7=makeQuery(id+"F17.imprint","IMPRINT",FACE,{"disambiguationData":[TD([[makeQuery(id+"F17.imprint","IMPRINT",EDGE,{"derivedFrom":sQuery(id+"F17.wireOp",EDGE,"E47")}),1.0]])]});
            extrude(context, id + "F21", {"entities" : qUnion([Q0, Q1, Q2, Q3, Q4, Q5, Q6, Q7]), "operationType" : NewBodyOperationType.ADD, "depth" : 1.6 * mm});
        }
        {
            var Q0;
            Q0=makeQuery(id+"F17.imprint","IMPRINT",FACE,{"disambiguationData":[TD([[makeQuery(id+"F17.imprint","IMPRINT",EDGE,{"derivedFrom":sQuery(id+"F17.wireOp",EDGE,"E66.bottom")}),1.0]])]});
            extrude(context, id + "F22", {"entities" : qUnion([Q0]), "operationType" : NewBodyOperationType.REMOVE, "oppositeDirection" : true, "depth" : 25 * mm});
        }
    });
